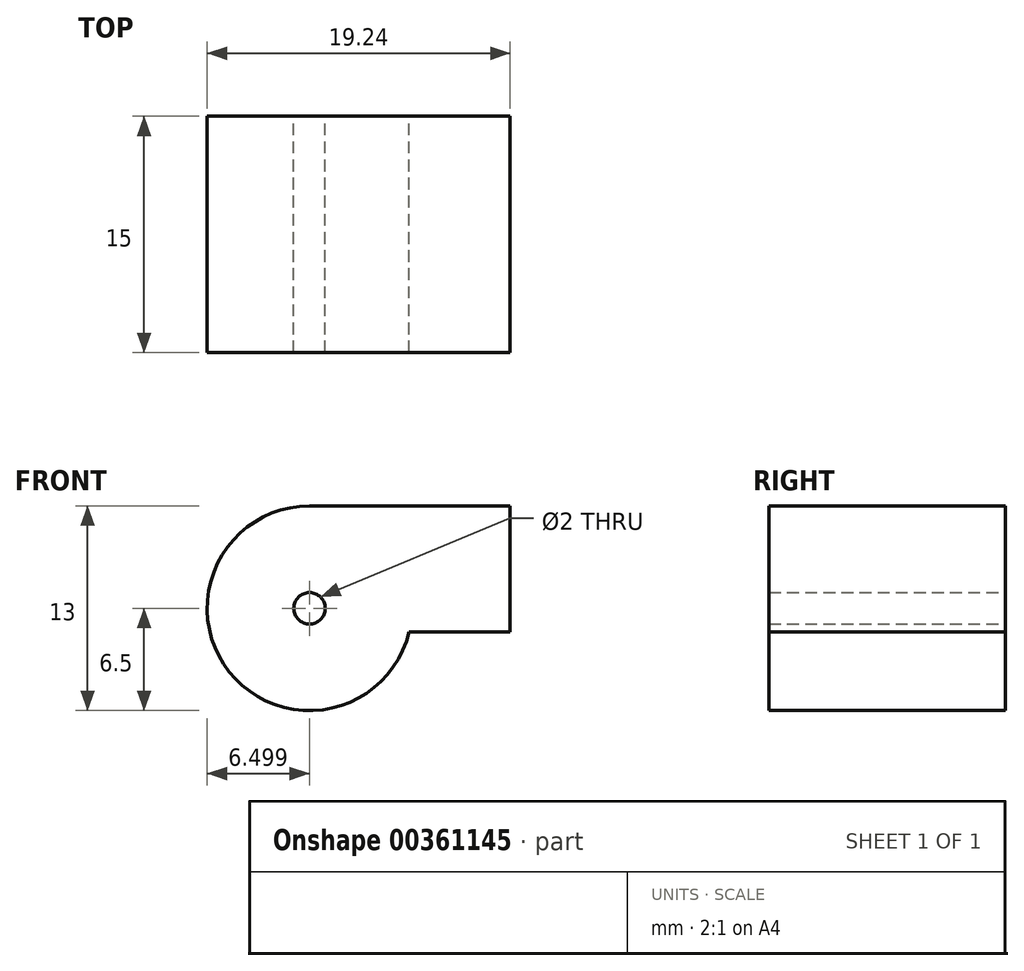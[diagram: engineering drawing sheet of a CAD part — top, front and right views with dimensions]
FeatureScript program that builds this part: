
annotation { "Feature Type Name" : "Feature", "Feature Type Description" : "" }
export const myFeature = defineFeature(function(context is Context, id is Id, definition is map)
    precondition{}
    {
        {
            var Q0;
            Q0=qCreatedBy(makeId("Front.planeOp"),FACE);
            var sketch = newSketch(context, id + "F0", { "sketchPlane" : qUnion([Q0])});
            skArc(sketch, "E0", {"start": v(-12.74, 6.5) * mm, "mid": v(-17.84, -4.03) * mm, "end": v(-6.42, -1.5) * mm});
            skArc(sketch, "E1.MirrorC", {"start": v(12.74, 6.5) * mm, "mid": v(17.84, -4.03) * mm, "end": v(6.42, -1.5) * mm});
            skLineSegment(sketch, "E2.bottom", {"start": v(-12.74, 6.5) * mm, "end": v(12.74, 6.5) * mm});
            skLineSegment(sketch, "E2.top", {"start": v(-6.42, -1.5) * mm, "end": v(6.42, -1.5) * mm});
            skPoint(sketch, "E3.orphan", {"position": v(12.74, -1.5) * mm});
            skCircle(sketch, "E4", {"center": v(-12.74, 0) * mm, "radius": 1 * mm});
            skCircle(sketch, "E5.MirrorC", {"center": v(12.74, 0) * mm, "radius": 1 * mm});
            skLineSegment(sketch, "E6", {"start": v(0, 6.5) * mm, "end": v(0, -1.5) * mm});
            skSolve(sketch);
        }
        {
            var Q0;
            Q0=makeQuery(id+"F0.imprint","IMPRINT",FACE,{"disambiguationData":[TD([[makeQuery(id+"F0.imprint","IMPRINT",EDGE,{"derivedFrom":sQuery(id+"F0.wireOp",EDGE,"E0")}),1.0]])]});
            extrude(context, id + "F1", {"entities" : qUnion([Q0]), "endBound" : BoundingType.SYMMETRIC, "depth" : 15 * mm});
        }
    });
